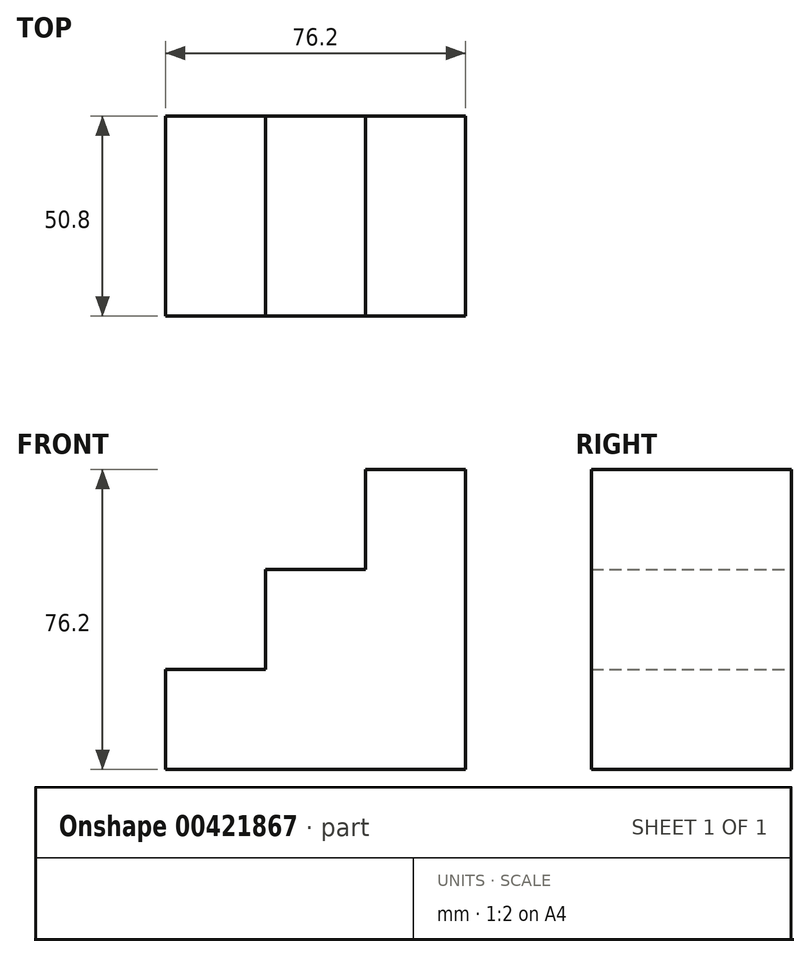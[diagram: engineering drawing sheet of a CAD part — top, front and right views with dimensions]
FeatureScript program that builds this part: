
annotation { "Feature Type Name" : "Feature", "Feature Type Description" : "" }
export const myFeature = defineFeature(function(context is Context, id is Id, definition is map)
    precondition{}
    {
        {
            var Q0;
            Q0=qCreatedBy(makeId("Front.planeOp"),FACE);
            var sketch = newSketch(context, id + "F0", { "sketchPlane" : qUnion([Q0])});
            skLineSegment(sketch, "E0", {"start": v(-51.46, 0) * mm, "end": v(24.74, 0) * mm});
            skLineSegment(sketch, "E1", {"start": v(24.74, 0) * mm, "end": v(24.74, 76.2) * mm});
            skLineSegment(sketch, "E2", {"start": v(24.74, 76.2) * mm, "end": v(-0.66, 76.2) * mm});
            skLineSegment(sketch, "E3", {"start": v(-0.66, 76.2) * mm, "end": v(-0.66, 50.8) * mm});
            skLineSegment(sketch, "E4", {"start": v(-0.66, 50.8) * mm, "end": v(-26.06, 50.8) * mm});
            skLineSegment(sketch, "E5", {"start": v(-26.06, 50.8) * mm, "end": v(-26.06, 25.4) * mm});
            skLineSegment(sketch, "E6", {"start": v(-26.06, 25.4) * mm, "end": v(-51.46, 25.4) * mm});
            skLineSegment(sketch, "E7", {"start": v(-51.46, 25.4) * mm, "end": v(-51.46, 0) * mm});
            skSolve(sketch);
        }
        {
            var Q0;
            Q0=makeQuery(id+"F0.imprint","IMPRINT",FACE,{"disambiguationData":[TD([[makeQuery(id+"F0.imprint","IMPRINT",EDGE,{"derivedFrom":sQuery(id+"F0.wireOp",EDGE,"E0")}),1.0]])]});
            extrude(context, id + "F1", {"entities" : qUnion([Q0]), "depth" : 50.8 * mm});
        }
    });
